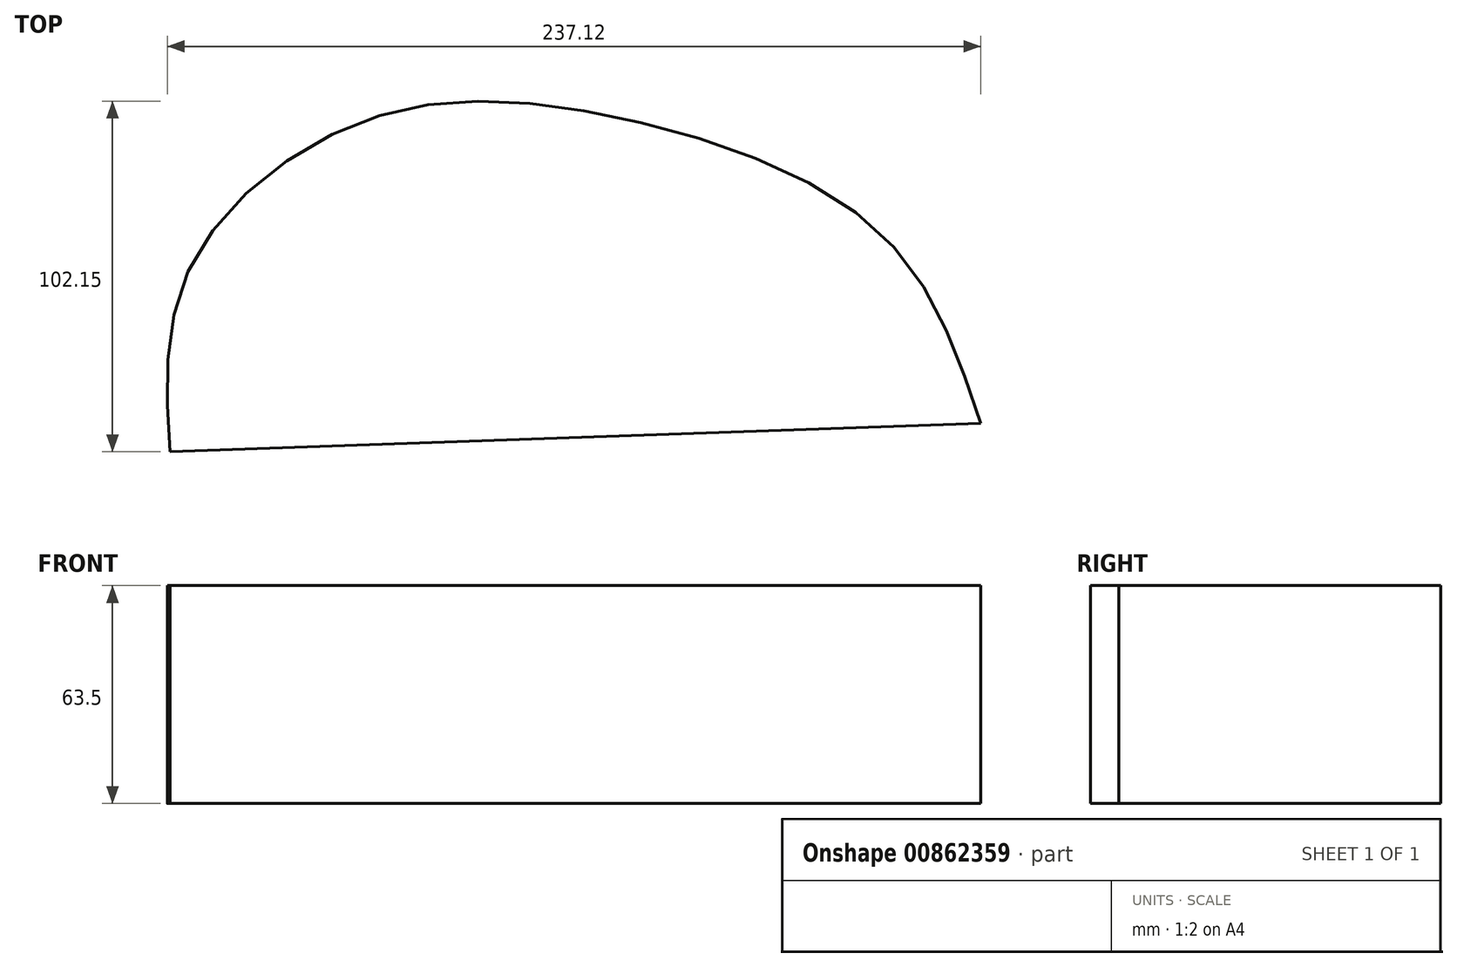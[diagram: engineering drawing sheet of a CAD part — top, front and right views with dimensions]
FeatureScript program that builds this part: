
annotation { "Feature Type Name" : "Feature", "Feature Type Description" : "" }
export const myFeature = defineFeature(function(context is Context, id is Id, definition is map)
    precondition{}
    {
        {
            var Q0;
            Q0=qCreatedBy(makeId("Top.planeOp"),FACE);
            var sketch = newSketch(context, id + "F0", { "sketchPlane" : qUnion([Q0])});
            skFitSpline(sketch, "E0", {"points": [v(-125.74, -8.25) * mm, v(-119.79, 45.64) * mm, v(-69.6, 88) * mm, v(0, 90.09) * mm, v(80.51, 56.26) * mm, v(110.62, 0) * mm], "startDerivative": vector(-18.53, 311.4) * mm, "endDerivative": vector(105.13, -317.2) * mm});
            skLineSegment(sketch, "E1", {"start": v(-125.74, -8.25) * mm, "end": v(110.62, 0) * mm});
            skSolve(sketch);
        }
        {
            var Q0;
            Q0=makeQuery(id+"F0.imprint","IMPRINT",FACE,{"disambiguationData":[TD([[makeQuery(id+"F0.imprint","IMPRINT",EDGE,{"derivedFrom":sQuery(id+"F0.wireOp",EDGE,"E0")}),-1.0]])]});
            extrude(context, id + "F1", {"entities" : qUnion([Q0]), "depth" : 63.5 * mm, "offsetDistance" : 25.4 * mm});
        }
    });
